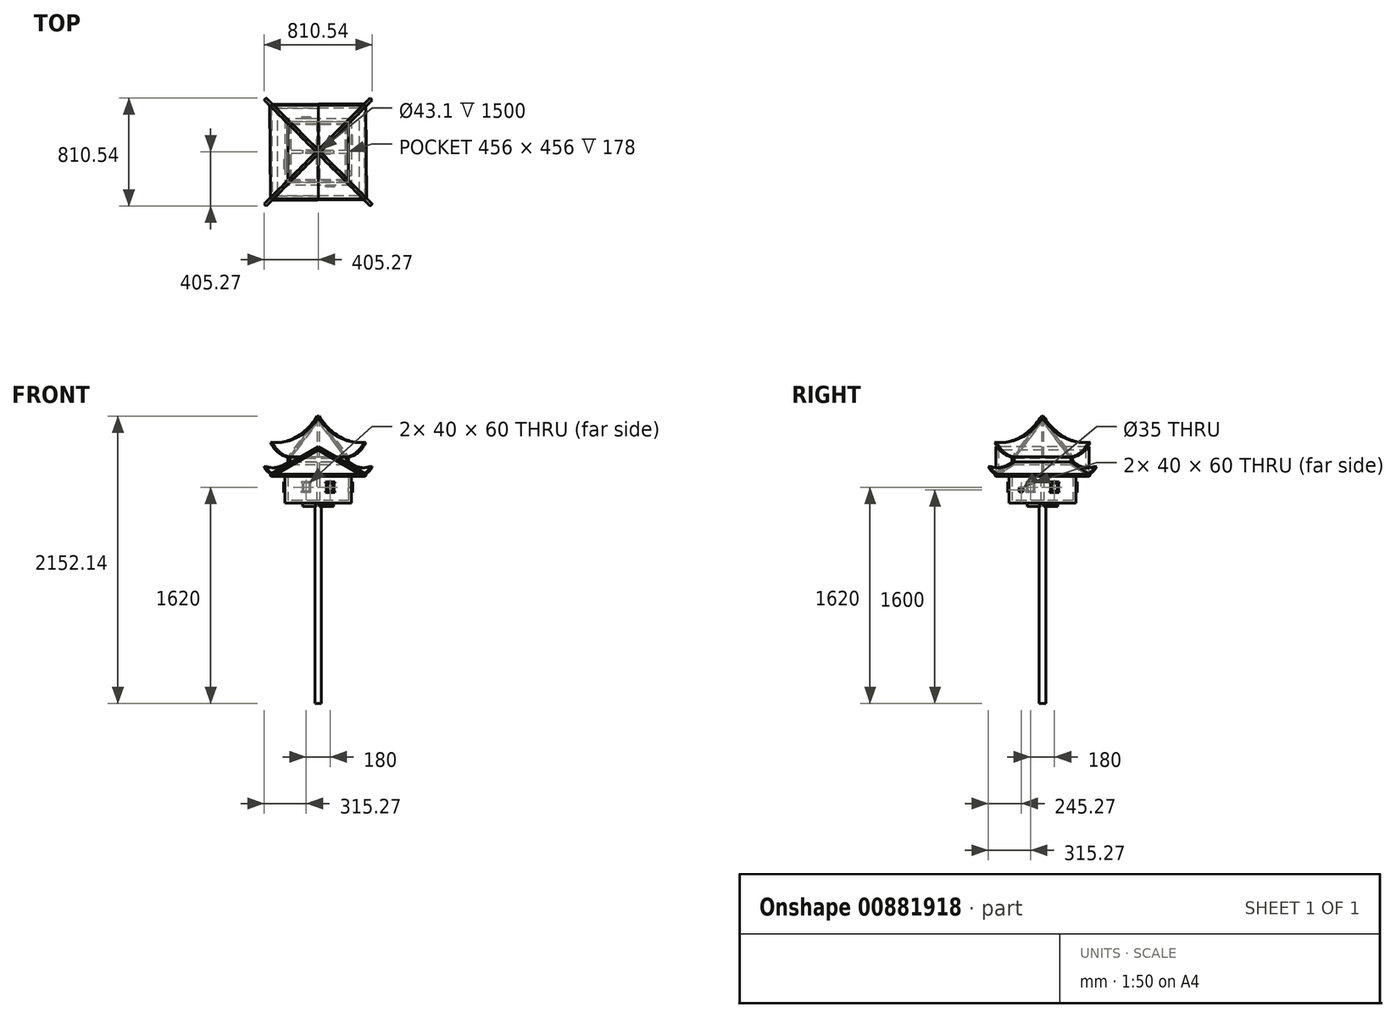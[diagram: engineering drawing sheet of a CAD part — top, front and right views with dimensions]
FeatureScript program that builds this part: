
annotation { "Feature Type Name" : "Feature", "Feature Type Description" : "" }
export const myFeature = defineFeature(function(context is Context, id is Id, definition is map)
    precondition{}
    {
        {
            var Q0;
            Q0=qCreatedBy(makeId("Top.planeOp"),FACE);
            var sketch = newSketch(context, id + "F0", { "sketchPlane" : qUnion([Q0])});
            skCircle(sketch, "E0", {"center": v(0, 0) * mm, "radius": 125 * mm, "construction": true});
            skCircle(sketch, "E1", {"center": v(0, -200) * mm, "radius": 24.15 * mm});
            skCircle(sketch, "E2", {"center": v(0, -200) * mm, "radius": 21.55 * mm});
            skSolve(sketch);
        }
        {
            var Q0;
            Q0 = qSketchRegion(id + "F0", true);
            extrude(context, id + "F1", {"entities" : qUnion([Q0]), "depth" : 1500 * mm, "offsetDistance" : 25 * mm});
        }
        {
            var Q0;
            Q0=qCreatedBy(makeId("Front.planeOp"),FACE);
            cPlane(context, id + "F2", {"entities" : qUnion([Q0]), "cplaneType" : CPlaneType.OFFSET, "offset" : 85 * mm, "width" : 150 * mm, "height" : 150 * mm});
        }
        {
            var Q0;
            Q0=qCreatedBy(id+"F2.planeOp",FACE);
            var sketch = newSketch(context, id + "F3", { "sketchPlane" : qUnion([Q0])});
            skLineSegment(sketch, "E3", {"start": v(-11.38, 1500) * mm, "end": v(-11.38, 1475) * mm});
            skLineSegment(sketch, "E4", {"start": v(-11.38, 1475) * mm, "end": v(-8.38, 1475) * mm});
            skLineSegment(sketch, "E5", {"start": v(-8.38, 1475) * mm, "end": v(-8.38, 1497) * mm});
            skLineSegment(sketch, "E6", {"start": v(-8.38, 1497) * mm, "end": v(13.62, 1497) * mm});
            skLineSegment(sketch, "E7", {"start": v(13.62, 1497) * mm, "end": v(13.62, 1500) * mm});
            skLineSegment(sketch, "E8", {"start": v(13.62, 1500) * mm, "end": v(-11.38, 1500) * mm});
            skSolve(sketch);
        }
        {
            var Q0;
            Q0 = qSketchRegion(id + "F3", true);
            extrude(context, id + "F4", {"entities" : qUnion([Q0]), "endBound" : BoundingType.UP_TO_NEXT, "depth" : 25 * mm, "offsetDistance" : 25 * mm});
        }
        {
            var Q0;
            Q0=makeQuery(id+"F4.opExtrude","SWEPT_BODY",BODY,{"disambiguationData":[OSD([sQuery(id+"F3.wireOp",EDGE,"E3"),sQuery(id+"F3.wireOp",EDGE,"E4"),sQuery(id+"F3.wireOp",EDGE,"E5"),sQuery(id+"F3.wireOp",EDGE,"E6"),sQuery(id+"F3.wireOp",EDGE,"E7"),sQuery(id+"F3.wireOp",EDGE,"E8")])]});
            var Q1;
            Q1=makeQuery(id+"F1.opExtrude","CAP_EDGE",EDGE,{"disambiguationData":[OSD([sQuery(id+"F0.wireOp",EDGE,"E1")])],"isStart":false});
            circularPattern(context, id + "F5", {"entities" : qUnion([Q0]), "axis" : qUnion([Q1]), "angle" : 360 * degree, "instanceCount" : 4, "equalSpace" : true});
        }
        {
            var Q0;
            Q0=makeQuery(id+"F4.opExtrude","SWEPT_FACE",FACE,{"disambiguationData":[OSD([sQuery(id+"F3.wireOp",EDGE,"E8")])]});
            var sketch = newSketch(context, id + "F6", { "sketchPlane" : qUnion([Q0])});
            skCircle(sketch, "E9.0", {"center": v(0, -200) * mm, "radius": 21.55 * mm, "construction": true});
            skLineSegment(sketch, "E10.bottom", {"start": v(250, 50) * mm, "end": v(-250, 50) * mm});
            skLineSegment(sketch, "E10.top", {"start": v(250, -450) * mm, "end": v(-250, -450) * mm});
            skLineSegment(sketch, "E10.left", {"start": v(250, 50) * mm, "end": v(250, -450) * mm});
            skLineSegment(sketch, "E10.right", {"start": v(-250, 50) * mm, "end": v(-250, -450) * mm});
            skSolve(sketch);
        }
        {
            var Q0;
            Q0 = qSketchRegion(id + "F6", true);
            extrude(context, id + "F7", {"entities" : qUnion([Q0]), "depth" : 200 * mm, "offsetDistance" : 25 * mm});
        }
        {
            var Q0;
            Q0=makeQuery(id+"F7.opExtrude","CAP_FACE",FACE,{"disambiguationData":[OSD([sQuery(id+"F6.wireOp",EDGE,"E10.bottom"),sQuery(id+"F6.wireOp",EDGE,"E10.top"),sQuery(id+"F6.wireOp",EDGE,"E10.left"),sQuery(id+"F6.wireOp",EDGE,"E10.right")])],"isStart":false});
            shell(context, id + "F8", {"entities" : qUnion([Q0]), "thickness" : 22 * mm});
        }
        {
            var Q0;
            Q0=makeQuery(id+"F8.opShell","OFFSET_FACE",FACE,{"disambiguationData":[OSD([sQuery(id+"F6.wireOp",EDGE,"E10.bottom"),sQuery(id+"F6.wireOp",EDGE,"E10.top"),sQuery(id+"F6.wireOp",EDGE,"E10.left"),sQuery(id+"F6.wireOp",EDGE,"E10.right")])]});
            var sketch = newSketch(context, id + "F9", { "sketchPlane" : qUnion([Q0])});
            skLineSegment(sketch, "E11.bottom", {"start": v(228, -189) * mm, "end": v(11, -189) * mm});
            skLineSegment(sketch, "E11.top", {"start": v(228, -211) * mm, "end": v(11, -211) * mm});
            skLineSegment(sketch, "E11.left", {"start": v(228, -189) * mm, "end": v(228, -211) * mm});
            skLineSegment(sketch, "E11.right", {"start": v(-228, -189) * mm, "end": v(-228, -211) * mm});
            skPoint(sketch, "E11.middle", {"position": v(0, -200) * mm});
            skPoint(sketch, "E11.middle.positionSnap0", {"position": v(-228, -200) * mm});
            skPoint(sketch, "E11.centerSnap0", {"position": v(-228, -200) * mm});
            skLineSegment(sketch, "E12.bottom", {"start": v(11, 28) * mm, "end": v(-11, 28) * mm});
            skLineSegment(sketch, "E12.top", {"start": v(11, -428) * mm, "end": v(-11, -428) * mm});
            skLineSegment(sketch, "E12.left", {"start": v(11, 28) * mm, "end": v(11, -189) * mm});
            skLineSegment(sketch, "E12.right", {"start": v(-11, 28) * mm, "end": v(-11, -189) * mm});
            skLineSegment(sketch, "E13.trimOffspring", {"start": v(11, -211) * mm, "end": v(11, -428) * mm});
            skLineSegment(sketch, "E14.trimOffspring", {"start": v(-11, -211) * mm, "end": v(-228, -211) * mm});
            skLineSegment(sketch, "E15.trimOffspring", {"start": v(-11, -211) * mm, "end": v(-11, -428) * mm});
            skLineSegment(sketch, "E16.trimOffspring", {"start": v(-11, -189) * mm, "end": v(-228, -189) * mm});
            skSolve(sketch);
        }
        {
            var Q0;
            Q0 = qSketchRegion(id + "F9", true);
            var Q1;
            Q1=makeQuery(id+"F7.opExtrude","CAP_FACE",FACE,{"disambiguationData":[OSD([sQuery(id+"F6.wireOp",EDGE,"E10.bottom"),sQuery(id+"F6.wireOp",EDGE,"E10.top"),sQuery(id+"F6.wireOp",EDGE,"E10.left"),sQuery(id+"F6.wireOp",EDGE,"E10.right")])],"isStart":false});
            extrude(context, id + "F10", {"entities" : qUnion([Q0]), "endBound" : BoundingType.UP_TO_SURFACE, "depth" : 25 * mm, "endBoundEntityFace" : qUnion([Q1]), "offsetDistance" : 25 * mm});
        }
        {
            var Q0;
            Q0=makeQuery(id+"F7.opExtrude","SWEPT_FACE",FACE,{"disambiguationData":[OSD([sQuery(id+"F6.wireOp",EDGE,"E10.left")])]});
            var sketch = newSketch(context, id + "F11", { "sketchPlane" : qUnion([Q0])});
            skCircle(sketch, "E17", {"center": v(-360, 1600) * mm, "radius": 17.5 * mm});
            skLineSegment(sketch, "E18", {"start": v(-450, 1600) * mm, "end": v(-360, 1600) * mm, "construction": true});
            skSolve(sketch);
        }
        {
            var Q0;
            Q0 = qSketchRegion(id + "F11", true);
            extrude(context, id + "F12", {"entities" : qUnion([Q0]), "operationType" : NewBodyOperationType.REMOVE, "oppositeDirection" : true, "depth" : 25 * mm, "offsetDistance" : 25 * mm});
        }
        {
            var Q0;
            Q0=makeQuery(id+"F10.opExtrude","CAP_FACE",FACE,{"disambiguationData":[OSD([sQuery(id+"F9.wireOp",EDGE,"E11.bottom"),sQuery(id+"F9.wireOp",EDGE,"E11.top"),sQuery(id+"F9.wireOp",EDGE,"E11.left"),sQuery(id+"F9.wireOp",EDGE,"E11.right"),sQuery(id+"F9.wireOp",EDGE,"E12.bottom"),sQuery(id+"F9.wireOp",EDGE,"E12.top"),sQuery(id+"F9.wireOp",EDGE,"E12.left"),sQuery(id+"F9.wireOp",EDGE,"E12.right"),sQuery(id+"F9.wireOp",EDGE,"E13.trimOffspring"),sQuery(id+"F9.wireOp",EDGE,"E14.trimOffspring"),sQuery(id+"F9.wireOp",EDGE,"E15.trimOffspring"),sQuery(id+"F9.wireOp",EDGE,"E16.trimOffspring")])],"isStart":false});
            var sketch = newSketch(context, id + "F13", { "sketchPlane" : qUnion([Q0])});
            skCircle(sketch, "E19.0", {"center": v(0, -200) * mm, "radius": 21.55 * mm, "construction": true});
            skLineSegment(sketch, "E20.bottom", {"start": v(350, -550) * mm, "end": v(-350, -550) * mm});
            skLineSegment(sketch, "E20.top", {"start": v(350, 150) * mm, "end": v(-350, 150) * mm});
            skLineSegment(sketch, "E20.left", {"start": v(350, -550) * mm, "end": v(350, 150) * mm});
            skLineSegment(sketch, "E20.right", {"start": v(-350, -550) * mm, "end": v(-350, 150) * mm});
            skSolve(sketch);
        }
        {
            var Q0;
            Q0 = qSketchRegion(id + "F13", true);
            extrude(context, id + "F14", {"entities" : qUnion([Q0]), "depth" : 22 * mm, "offsetDistance" : 25 * mm});
        }
        {
            var Q0;
            Q0=makeQuery(id+"F7.opExtrude","SWEPT_FACE",FACE,{"disambiguationData":[OSD([sQuery(id+"F6.wireOp",EDGE,"E10.top")])]});
            var sketch = newSketch(context, id + "F15", { "sketchPlane" : qUnion([Q0])});
            skLineSegment(sketch, "E21.bottom", {"start": v(60, 1650) * mm, "end": v(70, 1650) * mm});
            skLineSegment(sketch, "E21.top", {"start": v(60, 1590) * mm, "end": v(70, 1590) * mm});
            skLineSegment(sketch, "E21.left", {"start": v(60, 1650) * mm, "end": v(60, 1590) * mm});
            skLineSegment(sketch, "E21.right", {"start": v(70, 1650) * mm, "end": v(70, 1590) * mm});
            skLineSegment(sketch, "E22.bottom", {"start": v(110, 1650) * mm, "end": v(120, 1650) * mm});
            skLineSegment(sketch, "E22.top", {"start": v(110, 1590) * mm, "end": v(120, 1590) * mm});
            skLineSegment(sketch, "E22.left", {"start": v(110, 1650) * mm, "end": v(110, 1590) * mm});
            skLineSegment(sketch, "E22.right", {"start": v(120, 1650) * mm, "end": v(120, 1590) * mm});
            skLineSegment(sketch, "E23.bottom", {"start": v(55, 1660) * mm, "end": v(125, 1660) * mm});
            skLineSegment(sketch, "E23.top", {"start": v(55, 1650) * mm, "end": v(125, 1650) * mm});
            skLineSegment(sketch, "E23.left", {"start": v(55, 1660) * mm, "end": v(55, 1650) * mm});
            skLineSegment(sketch, "E23.right", {"start": v(125, 1660) * mm, "end": v(125, 1650) * mm});
            skLineSegment(sketch, "E24.bottom", {"start": v(55, 1580) * mm, "end": v(125, 1580) * mm});
            skLineSegment(sketch, "E24.top", {"start": v(55, 1590) * mm, "end": v(125, 1590) * mm});
            skLineSegment(sketch, "E24.left", {"start": v(55, 1580) * mm, "end": v(55, 1590) * mm});
            skLineSegment(sketch, "E24.right", {"start": v(125, 1580) * mm, "end": v(125, 1590) * mm});
            skSolve(sketch);
        }
        {
            var Q0;
            Q0 = qSketchRegion(id + "F15", true);
            extrude(context, id + "F16", {"entities" : qUnion([Q0]), "depth" : 10 * mm, "offsetDistance" : 25 * mm});
        }
        {
            var Q0;
            Q0=makeQuery(id+"F16.opExtrude","SWEPT_BODY",BODY,{"disambiguationData":[OSD([sQuery(id+"F15.wireOp",EDGE,"E21.left"),sQuery(id+"F15.wireOp",EDGE,"E21.right"),sQuery(id+"F15.wireOp",EDGE,"E22.left"),sQuery(id+"F15.wireOp",EDGE,"E22.right"),sQuery(id+"F15.wireOp",EDGE,"E23.bottom"),sQuery(id+"F15.wireOp",EDGE,"E23.top"),sQuery(id+"F15.wireOp",EDGE,"E23.left"),sQuery(id+"F15.wireOp",EDGE,"E23.right"),sQuery(id+"F15.wireOp",EDGE,"E24.bottom"),sQuery(id+"F15.wireOp",EDGE,"E24.top"),sQuery(id+"F15.wireOp",EDGE,"E24.left"),sQuery(id+"F15.wireOp",EDGE,"E24.right")])]});
            var Q1;
            Q1=makeQuery(id+"F1.opExtrude","CAP_EDGE",EDGE,{"disambiguationData":[OSD([sQuery(id+"F0.wireOp",EDGE,"E2")])],"isStart":true});
            circularPattern(context, id + "F17", {"entities" : qUnion([Q0]), "axis" : qUnion([Q1]), "angle" : 360 * degree, "instanceCount" : 4, "equalSpace" : true});
        }
        {
            var Q0;
            Q0=makeQuery(id+"F14.opExtrude","SWEPT_FACE",FACE,{"disambiguationData":[OSD([sQuery(id+"F13.wireOp",EDGE,"E20.bottom")])]});
            var sketch = newSketch(context, id + "F18", { "sketchPlane" : qUnion([Q0])});
            skLineSegment(sketch, "E25", {"start": v(0, 1924.07) * mm, "end": v(-350, 1722) * mm});
            skLineSegment(sketch, "E26", {"start": v(-350, 1722) * mm, "end": v(-306, 1722) * mm});
            skLineSegment(sketch, "E27", {"start": v(-306, 1722) * mm, "end": v(0, 1898.67) * mm});
            skLineSegment(sketch, "E28", {"start": v(0, 1898.67) * mm, "end": v(0, 1924.07) * mm});
            skSolve(sketch);
        }
        {
            var Q0;
            Q0 = qSketchRegion(id + "F18", true);
            var Q1;
            Q1=makeQuery(id+"F14.opExtrude","SWEPT_FACE",FACE,{"disambiguationData":[OSD([sQuery(id+"F13.wireOp",EDGE,"E20.top")])]});
            extrude(context, id + "F19", {"entities" : qUnion([Q0]), "endBound" : BoundingType.UP_TO_SURFACE, "oppositeDirection" : true, "depth" : 25 * mm, "endBoundEntityFace" : qUnion([Q1]), "offsetDistance" : 25 * mm});
        }
        {
            var Q0;
            Q0=makeQuery(id+"F19.opExtrude","SWEPT_BODY",BODY,{"disambiguationData":[OSD([sQuery(id+"F18.wireOp",EDGE,"E25"),sQuery(id+"F18.wireOp",EDGE,"E26"),sQuery(id+"F18.wireOp",EDGE,"E27"),sQuery(id+"F18.wireOp",EDGE,"E28")])]});
            var Q1;
            Q1=qCreatedBy(makeId("Right.planeOp"),FACE);
            mirror(context, id + "F20", {"entities" : qUnion([Q0]), "mirrorPlane" : qUnion([Q1])});
        }
        {
            var Q0;
            Q0=makeQuery(id+"F14.opExtrude","SWEPT_FACE",FACE,{"disambiguationData":[OSD([sQuery(id+"F13.wireOp",EDGE,"E20.bottom")])]});
            var sketch = newSketch(context, id + "F21", { "sketchPlane" : qUnion([Q0])});
            skLineSegment(sketch, "E29.0", {"start": v(-306, 1722) * mm, "end": v(0, 1898.67) * mm});
            skLineSegment(sketch, "E30.0", {"start": v(306, 1722) * mm, "end": v(0, 1898.67) * mm});
            skLineSegment(sketch, "E31.0", {"start": v(350, 1722) * mm, "end": v(-350, 1722) * mm});
            skSolve(sketch);
        }
        {
            var Q0;
            Q0 = qSketchRegion(id + "F21", true);
            extrude(context, id + "F22", {"entities" : qUnion([Q0]), "oppositeDirection" : true, "depth" : 22 * mm, "offsetDistance" : 25 * mm});
        }
        {
            var Q0;
            Q0=makeQuery(id+"F7.opExtrude","SWEPT_FACE",FACE,{"disambiguationData":[OSD([sQuery(id+"F6.wireOp",EDGE,"E10.top")])]});
            var Q1;
            Q1=makeQuery(id+"F7.opExtrude","SWEPT_FACE",FACE,{"disambiguationData":[OSD([sQuery(id+"F6.wireOp",EDGE,"E10.bottom")])]});
            cPlane(context, id + "F23", {"entities" : qUnion([Q0, Q1]), "cplaneType" : CPlaneType.MID_PLANE, "offset" : 25 * mm, "width" : 150 * mm, "height" : 150 * mm});
        }
        {
            var Q0;
            Q0=makeQuery(id+"F22.opExtrude","SWEPT_BODY",BODY,{"disambiguationData":[OSD([sQuery(id+"F21.wireOp",EDGE,"E29.0"),sQuery(id+"F21.wireOp",EDGE,"E30.0"),sQuery(id+"F21.wireOp",EDGE,"E31.0")])]});
            var Q1;
            Q1=qCreatedBy(id+"F23.planeOp",FACE);
            mirror(context, id + "F24", {"entities" : qUnion([Q0]), "mirrorPlane" : qUnion([Q1])});
        }
        {
            var Q0;
            Q0=makeQuery(id+"F7.opExtrude","SWEPT_FACE",FACE,{"disambiguationData":[OSD([sQuery(id+"F6.wireOp",EDGE,"E10.right")])]});
            var Q1;
            Q1=makeQuery(id+"F7.opExtrude","SWEPT_FACE",FACE,{"disambiguationData":[OSD([sQuery(id+"F6.wireOp",EDGE,"E10.left")])]});
            cPlane(context, id + "F25", {"entities" : qUnion([Q0, Q1]), "cplaneType" : CPlaneType.MID_PLANE, "offset" : 25 * mm, "width" : 150 * mm, "height" : 150 * mm});
        }
        {
            var Q0;
            Q0=qCreatedBy(id+"F25.planeOp",FACE);
            var Q1;
            Q1=qCreatedBy(id+"F23.planeOp",FACE);
            cPlane(context, id + "F26", {"entities" : qUnion([Q0, Q1]), "cplaneType" : CPlaneType.MID_PLANE, "offset" : 25 * mm, "width" : 150 * mm, "height" : 150 * mm});
        }
        {
            var Q0;
            Q0=qCreatedBy(id+"F26.planeOp",FACE);
            var sketch = newSketch(context, id + "F27", { "sketchPlane" : qUnion([Q0])});
            skLineSegment(sketch, "E32", {"start": v(141.42, 2152.14) * mm, "end": v(141.42, 1722) * mm});
            skArc(sketch, "E33", {"start": v(141.42, 2152.14) * mm, "mid": v(365.99, 1996.27) * mm, "end": v(636.4, 1956.2) * mm});
            skArc(sketch, "E34", {"start": v(451.32, 1846.57) * mm, "mid": v(556.25, 1880.46) * mm, "end": v(636.4, 1956.2) * mm});
            skArc(sketch, "E35", {"start": v(452.15, 1810.14) * mm, "mid": v(574.58, 1769.11) * mm, "end": v(703.55, 1775.27) * mm});
            skArc(sketch, "E36", {"start": v(636.4, 1722) * mm, "mid": v(674.68, 1742.7) * mm, "end": v(703.55, 1775.27) * mm});
            skLineSegment(sketch, "E37", {"start": v(451.32, 1846.57) * mm, "end": v(452.15, 1810.14) * mm});
            skLineSegment(sketch, "E38", {"start": v(636.4, 1722) * mm, "end": v(141.42, 1722) * mm});
            skSolve(sketch);
        }
        {
            var Q0;
            Q0 = qSketchRegion(id + "F27", true);
            extrude(context, id + "F28", {"entities" : qUnion([Q0]), "endBound" : BoundingType.SYMMETRIC, "depth" : 22 * mm, "offsetDistance" : 25 * mm});
        }
        {
            var Q0;
            Q0=makeQuery(id+"F28.opExtrude","SWEPT_BODY",BODY,{"disambiguationData":[OSD([sQuery(id+"F27.wireOp",EDGE,"E32"),sQuery(id+"F27.wireOp",EDGE,"E33"),sQuery(id+"F27.wireOp",EDGE,"E34"),sQuery(id+"F27.wireOp",EDGE,"E35"),sQuery(id+"F27.wireOp",EDGE,"E36"),sQuery(id+"F27.wireOp",EDGE,"E37"),sQuery(id+"F27.wireOp",EDGE,"E38")])]});
            var Q1;
            Q1=makeQuery(id+"F1.opExtrude","CAP_EDGE",EDGE,{"disambiguationData":[OSD([sQuery(id+"F0.wireOp",EDGE,"E1")])],"isStart":true});
            circularPattern(context, id + "F29", {"entities" : qUnion([Q0]), "axis" : qUnion([Q1]), "angle" : 360 * degree, "instanceCount" : 4, "equalSpace" : true});
        }
        {
            var Q0;
            Q0=makeQuery(id+"F28.opExtrude","CAP_VERTEX",VERTEX,{"disambiguationData":[OSD([sQuery(id+"F27.wireOp",EDGE,"E34"),sQuery(id+"F27.wireOp",EDGE,"E37")])],"isStart":true});
            var Q1;
            Q1=makeQuery(id+"F28.opExtrude","CAP_VERTEX",VERTEX,{"disambiguationData":[OSD([sQuery(id+"F27.wireOp",EDGE,"E35"),sQuery(id+"F27.wireOp",EDGE,"E37")])],"isStart":true});
            var Q2;
            Q2=makeQuery(id+"F29.opPattern","COPY",VERTEX,{"derivedFrom":makeQuery(id+"F28.opExtrude","CAP_VERTEX",VERTEX,{"disambiguationData":[OSD([sQuery(id+"F27.wireOp",EDGE,"E34"),sQuery(id+"F27.wireOp",EDGE,"E37")])],"isStart":false}),"instanceName":"1"});
            cPlane(context, id + "F30", {"entities" : qUnion([Q0, Q1, Q2]), "cplaneType" : CPlaneType.THREE_POINT, "offset" : 25 * mm, "width" : 150 * mm, "height" : 150 * mm});
        }
        {
            var Q0;
            Q0=qCreatedBy(id+"F30.planeOp",FACE);
            var sketch = newSketch(context, id + "F31", { "sketchPlane" : qUnion([Q0])});
            skLineSegment(sketch, "E39.bottom", {"start": v(211.36, 1839.52) * mm, "end": v(-211.94, 1839.52) * mm});
            skLineSegment(sketch, "E39.top", {"start": v(211.36, 1803.08) * mm, "end": v(-211.94, 1803.08) * mm});
            skLineSegment(sketch, "E39.left", {"start": v(211.36, 1839.52) * mm, "end": v(211.36, 1803.08) * mm});
            skLineSegment(sketch, "E39.right", {"start": v(-211.94, 1839.52) * mm, "end": v(-211.94, 1803.08) * mm});
            skSolve(sketch);
        }
        {
            var Q0;
            Q0 = qSketchRegion(id + "F31", true);
            extrude(context, id + "F32", {"entities" : qUnion([Q0]), "depth" : 22 * mm, "offsetDistance" : 25 * mm});
        }
        {
            var Q0;
            Q0=makeQuery(id+"F28.opExtrude","SWEPT_EDGE",EDGE,{"disambiguationData":[OSD([sQuery(id+"F27.wireOp",EDGE,"E32"),sQuery(id+"F27.wireOp",EDGE,"E33")])]});
            cPoint(context, id + "F33", {"entities" : qUnion([Q0]), "parameter" : 0.5});
        }
        {
            var Q0;
            Q0 = qCreatedBy(id + "F33" ,VERTEX);
            var Q1;
            Q1=makeQuery(id+"F28.opExtrude","CAP_VERTEX",VERTEX,{"disambiguationData":[OSD([sQuery(id+"F27.wireOp",EDGE,"E34"),sQuery(id+"F27.wireOp",EDGE,"E37")])],"isStart":true});
            var Q2;
            Q2=makeQuery(id+"F32.opExtrude","CAP_VERTEX",VERTEX,{"disambiguationData":[OSD([sQuery(id+"F31.wireOp",EDGE,"E39.bottom"),sQuery(id+"F31.wireOp",EDGE,"E39.right")])],"isStart":true});
            cPlane(context, id + "F34", {"entities" : qUnion([Q0, Q1, Q2]), "cplaneType" : CPlaneType.THREE_POINT, "offset" : 25 * mm, "width" : 150 * mm, "height" : 150 * mm});
        }
        {
            var Q0;
            Q0=qCreatedBy(id+"F34.planeOp",FACE);
            var sketch = newSketch(context, id + "F35", { "sketchPlane" : qUnion([Q0])});
            skLineSegment(sketch, "E40", {"start": v(0, 1608.6) * mm, "end": v(211.36, 1228) * mm});
            skLineSegment(sketch, "E41", {"start": v(211.36, 1228) * mm, "end": v(-211.36, 1228) * mm});
            skLineSegment(sketch, "E42", {"start": v(-211.36, 1228) * mm, "end": v(0, 1608.6) * mm});
            skSolve(sketch);
        }
        {
            var Q0;
            Q0 = qSketchRegion(id + "F35", true);
            extrude(context, id + "F36", {"entities" : qUnion([Q0]), "depth" : 22 * mm, "offsetDistance" : 25 * mm});
        }
        {
            var Q0;
            Q0=makeQuery(id+"F28.opExtrude","CAP_VERTEX",VERTEX,{"disambiguationData":[OSD([sQuery(id+"F27.wireOp",EDGE,"E36"),sQuery(id+"F27.wireOp",EDGE,"E38")])],"isStart":true});
            var Q1;
            Q1=makeQuery(id+"F32.opExtrude","CAP_VERTEX",VERTEX,{"disambiguationData":[OSD([sQuery(id+"F31.wireOp",EDGE,"E39.top"),sQuery(id+"F31.wireOp",EDGE,"E39.left")])],"isStart":true});
            var Q2;
            Q2=makeQuery(id+"F29.opPattern","COPY",VERTEX,{"derivedFrom":makeQuery(id+"F28.opExtrude","CAP_VERTEX",VERTEX,{"disambiguationData":[OSD([sQuery(id+"F27.wireOp",EDGE,"E35"),sQuery(id+"F27.wireOp",EDGE,"E37")])],"isStart":false}),"instanceName":"1"});
            cPlane(context, id + "F37", {"entities" : qUnion([Q0, Q1, Q2]), "cplaneType" : CPlaneType.THREE_POINT, "offset" : 25 * mm, "width" : 150 * mm, "height" : 150 * mm});
        }
        {
            var Q0;
            Q0=qCreatedBy(id+"F37.planeOp",FACE);
            var sketch = newSketch(context, id + "F38", { "sketchPlane" : qUnion([Q0])});
            skLineSegment(sketch, "E43", {"start": v(-211.94, 660.17) * mm, "end": v(-350, 496.99) * mm});
            skLineSegment(sketch, "E44", {"start": v(-350, 496.99) * mm, "end": v(342.22, 502.87) * mm});
            skLineSegment(sketch, "E45", {"start": v(342.22, 502.87) * mm, "end": v(211.94, 660.17) * mm});
            skLineSegment(sketch, "E46", {"start": v(211.94, 660.17) * mm, "end": v(-211.94, 660.17) * mm});
            skSolve(sketch);
        }
        {
            var Q0;
            Q0 = qSketchRegion(id + "F38", true);
            extrude(context, id + "F39", {"entities" : qUnion([Q0]), "oppositeDirection" : true, "depth" : 22 * mm, "offsetDistance" : 25 * mm});
        }
        {
            var Q0;
            Q0=makeQuery(id+"F39.opExtrude","SWEPT_BODY",BODY,{"disambiguationData":[OSD([sQuery(id+"F38.wireOp",EDGE,"E43"),sQuery(id+"F38.wireOp",EDGE,"E44"),sQuery(id+"F38.wireOp",EDGE,"E45"),sQuery(id+"F38.wireOp",EDGE,"E46")])]});
            var Q1;
            Q1=makeQuery(id+"F32.opExtrude","SWEPT_BODY",BODY,{"disambiguationData":[OSD([sQuery(id+"F31.wireOp",EDGE,"E39.bottom"),sQuery(id+"F31.wireOp",EDGE,"E39.top"),sQuery(id+"F31.wireOp",EDGE,"E39.left"),sQuery(id+"F31.wireOp",EDGE,"E39.right")])]});
            var Q2;
            Q2=makeQuery(id+"F36.opExtrude","SWEPT_BODY",BODY,{"disambiguationData":[OSD([sQuery(id+"F35.wireOp",EDGE,"E40"),sQuery(id+"F35.wireOp",EDGE,"E41"),sQuery(id+"F35.wireOp",EDGE,"E42")])]});
            var Q3;
            Q3=makeQuery(id+"F1.opExtrude","CAP_EDGE",EDGE,{"disambiguationData":[OSD([sQuery(id+"F0.wireOp",EDGE,"E1")])],"isStart":true});
            circularPattern(context, id + "F40", {"entities" : qUnion([Q0, Q1, Q2]), "axis" : qUnion([Q3]), "angle" : 360 * degree, "instanceCount" : 4, "equalSpace" : true});
        }
    });
